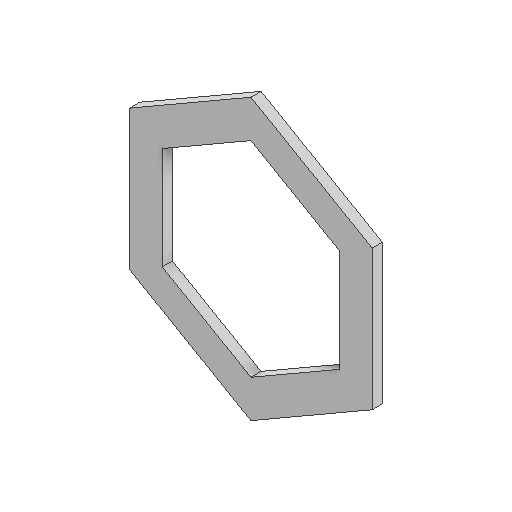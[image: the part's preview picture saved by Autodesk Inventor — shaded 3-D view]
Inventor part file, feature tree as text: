
AUTODESK INVENTOR PART (.ipt)
format: ipt  version: 2024.1 (Build 281209000, 209)  size: 95,744 bytes
history: native  units: mm
features: extrude x1, sketch x1
ambient origin geometry x8: Origin, YZ Plane, XZ Plane, XY Plane, X Axis, Y Axis, Z Axis, Center Point
bodies: Solid1 (feature_tree)
feature tree (2):
  extrude  "Extrusion1"  Depth=2.4mm
  sketch  "Sketch1"  dims[d0=13.1mm d1=2.4mm d2=0.75mm d3=0.0mm]
